# Revit family: KL Rost D – E
name_source: partatom
category: Sanitärinstallationen
revit_build: Autodesk Revit Architecture 2016 (Build: 20150220_1215(x64)
units: mm (PartAtom-declared; Revit-internal decimal feet)

## family parameters
Arbeitsebenenbasiert = Nein
Beim Laden mit Abzugskörper schneiden = Nein
Bemaßung runder Anschluss = Durchmesser verwenden
Gemeinsam genutzt = Nein
Immer vertikal = Ja
OmniClass-Nummer = 23.45.00.00
OmniClass-Titel = Sanitary, Laundry, and Cleaning Equipment
Raumberechnungspunkt = Nein
Teiletyp = Normal

## types (14) — shared parameters
Height = 12 mm  [stored 0.0393701 ft]

## per-type parameters (varying)
| type | Length |
| KLD E 50 | 490 mm  [stored 1.60761 ft] |
| KLD E 60 | 590 mm  [stored 1.9357 ft] |
| KLD E 70 | 690 mm  [stored 2.26378 ft] |
| KLD E 80 | 790 mm  [stored 2.59186 ft] |
| KLD E 90 | 890 mm  [stored 2.91995 ft] |
| KLD E 100 | 990 mm  [stored 3.24803 ft] |
| KLD E 110 | 1090 mm  [stored 3.57612 ft] |
| KLD E 120 | 1190 mm  [stored 3.9042 ft] |
| KLD E 130 | 1290 mm  [stored 4.23228 ft] |
| KLD E 140 | 1390 mm  [stored 4.56037 ft] |
| KLD E 150 | 1490 mm  [stored 4.88845 ft] |
| KLD E 160 | 1590 mm  [stored 5.21654 ft] |
| KLD E 170 | 1690 mm  [stored 5.54462 ft] |
| KLD E 180 | 1790 mm  [stored 5.8727 ft] |

note: [stored X ft] marks values corroborated as IEEE doubles in the binary element streams (Revit-internal decimal feet)

## geometry (parser evidence)
native form markers: Sweep x2
no freeform markers — native parametric forms only
